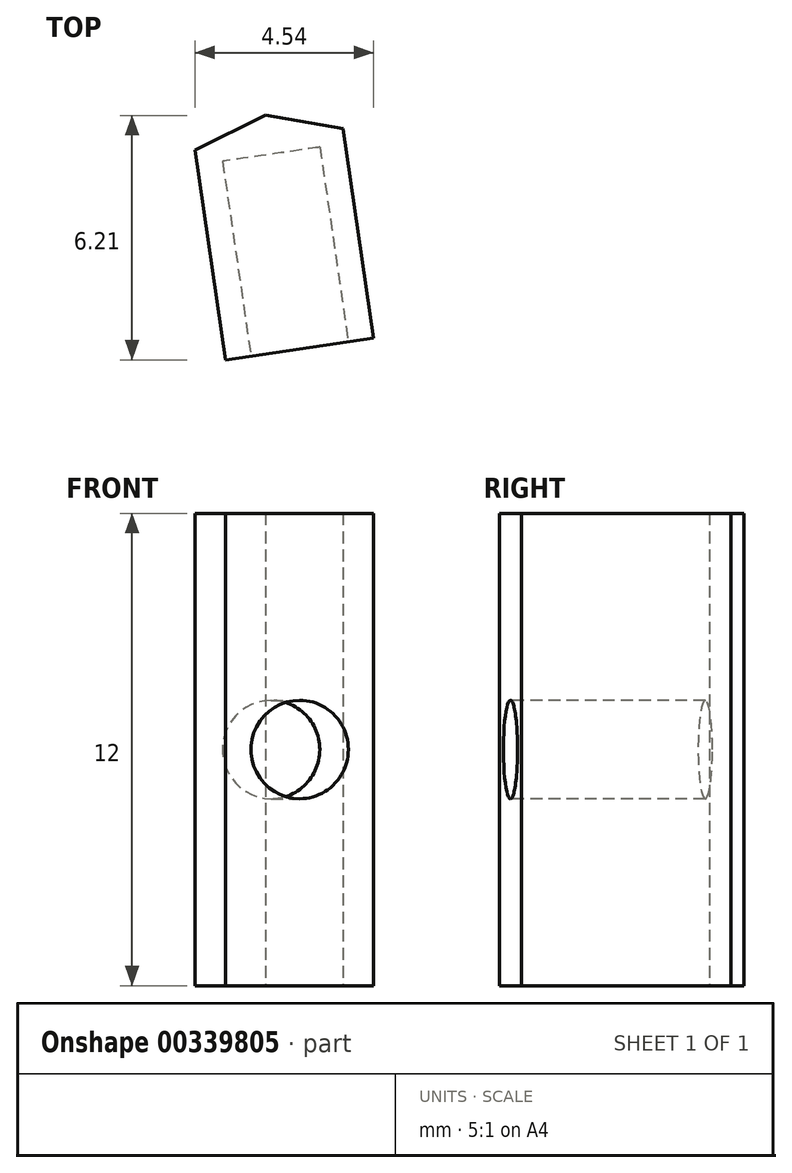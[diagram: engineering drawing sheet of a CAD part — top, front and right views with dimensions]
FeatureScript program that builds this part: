
annotation { "Feature Type Name" : "Feature", "Feature Type Description" : "" }
export const myFeature = defineFeature(function(context is Context, id is Id, definition is map)
    precondition{}
    {
        {
            var Q0;
            Q0=qCreatedBy(makeId("Top.planeOp"),FACE);
            var sketch = newSketch(context, id + "F0", { "sketchPlane" : qUnion([Q0])});
            skCircle(sketch, "E0", {"center": v(0, 0) * mm, "radius": 9.25 * mm});
            skCircle(sketch, "E1.cCircle", {"center": v(0, 0) * mm, "radius": 9.25 * mm, "construction": true});
            skLineSegment(sketch, "E1.0", {"start": v(9.59, -1.63) * mm, "end": v(6.8, -6.96) * mm});
            skLineSegment(sketch, "E1.1", {"start": v(6.8, -6.96) * mm, "end": v(1.4, -9.62) * mm});
            skLineSegment(sketch, "E1.2", {"start": v(1.4, -9.62) * mm, "end": v(-4.52, -8.61) * mm});
            skLineSegment(sketch, "E1.3", {"start": v(-4.52, -8.61) * mm, "end": v(-8.72, -4.31) * mm});
            skLineSegment(sketch, "E1.4", {"start": v(-8.72, -4.31) * mm, "end": v(-9.59, 1.63) * mm});
            skLineSegment(sketch, "E1.5", {"start": v(-9.59, 1.63) * mm, "end": v(-6.8, 6.96) * mm});
            skLineSegment(sketch, "E1.6", {"start": v(-6.8, 6.96) * mm, "end": v(-1.4, 9.62) * mm});
            skLineSegment(sketch, "E1.7", {"start": v(-1.4, 9.62) * mm, "end": v(4.52, 8.61) * mm});
            skLineSegment(sketch, "E1.8", {"start": v(4.52, 8.61) * mm, "end": v(8.72, 4.31) * mm});
            skLineSegment(sketch, "E1.9", {"start": v(8.72, 4.31) * mm, "end": v(9.59, -1.63) * mm});
            skPoint(sketch, "E1.0.midPoint", {"position": v(8.2, -4.3) * mm});
            skLineSegment(sketch, "E2", {"start": v(-1.4, 9.62) * mm, "end": v(0, 0) * mm});
            skLineSegment(sketch, "E3", {"start": v(-0.54, 3.69) * mm, "end": v(1.34, 3.96) * mm});
            skLineSegment(sketch, "E4", {"start": v(1.34, 3.96) * mm, "end": v(0.56, 9.29) * mm});
            skLineSegment(sketch, "E5", {"start": v(-0.54, 3.69) * mm, "end": v(-2.42, 3.41) * mm});
            skLineSegment(sketch, "E6", {"start": v(-2.42, 3.41) * mm, "end": v(-3.2, 8.74) * mm});
            skSolve(sketch);
        }
        {
            var Q0;
            {var subQ5=sQuery(id+"F0.wireOp",EDGE,"E5");Q0=makeQuery(id+"F0.imprint","IMPRINT",FACE,{"disambiguationData":[TD([[makeQuery(id+"F0.imprint","IMPRINT",EDGE,{"derivedFrom":subQ5}),-1.0]])]});}
            var Q1;
            {var subQ5=sQuery(id+"F0.wireOp",EDGE,"E3");Q1=makeQuery(id+"F0.imprint","IMPRINT",FACE,{"disambiguationData":[TD([[makeQuery(id+"F0.imprint","IMPRINT",EDGE,{"derivedFrom":subQ5}),1.0]])]});}
            var Q2;
            {var subQ0=sQuery(id+"F0.wireOp",EDGE,"E4");var subQ1=sQuery(id+"F0.wireOp",EDGE,"E0");var subQ2=makeQuery(id+"F0.imprint","INTERSECT",VERTEX,{"derivedFrom":[subQ1,subQ0]});Q2=makeQuery(id+"F0.imprint","IMPRINT",FACE,{"disambiguationData":[TD([[makeQuery(id+"F0.imprint","IMPRINT",EDGE,{"disambiguationData":[TD([[subQ2,-1.0]])],"derivedFrom":subQ1}),-1.0]])]});}
            var Q3;
            {var subQ0=sQuery(id+"F0.wireOp",EDGE,"E2");var subQ1=sQuery(id+"F0.wireOp",EDGE,"E0");var subQ2=makeQuery(id+"F0.imprint","INTERSECT",VERTEX,{"derivedFrom":[subQ1,subQ0]});Q3=makeQuery(id+"F0.imprint","IMPRINT",FACE,{"disambiguationData":[TD([[makeQuery(id+"F0.imprint","IMPRINT",EDGE,{"disambiguationData":[TD([[subQ2,-1.0]])],"derivedFrom":subQ1}),-1.0]])]});}
            extrude(context, id + "F1", {"entities" : qUnion([Q0, Q1, Q2, Q3]), "depth" : 12 * mm});
        }
        {
            var Q0;
            Q0=makeQuery(id+"F1.opExtrude","SWEPT_FACE",FACE,{"disambiguationData":[OSD([sQuery(id+"F0.wireOp",EDGE,"E3"),sQuery(id+"F0.wireOp",EDGE,"E5")])]});
            var sketch = newSketch(context, id + "F2", { "sketchPlane" : qUnion([Q0])});
            skCircle(sketch, "E7", {"center": v(0, 6) * mm, "radius": 1.25 * mm});
            skPoint(sketch, "E7.centerSnap0", {"position": v(-1.9, 6) * mm});
            skSolve(sketch);
        }
        {
            var Q0;
            Q0 = qSketchRegion(id + "F2", true);
            extrude(context, id + "F3", {"entities" : qUnion([Q0]), "operationType" : NewBodyOperationType.REMOVE, "oppositeDirection" : true, "depth" : 5 * mm});
        }
    });
